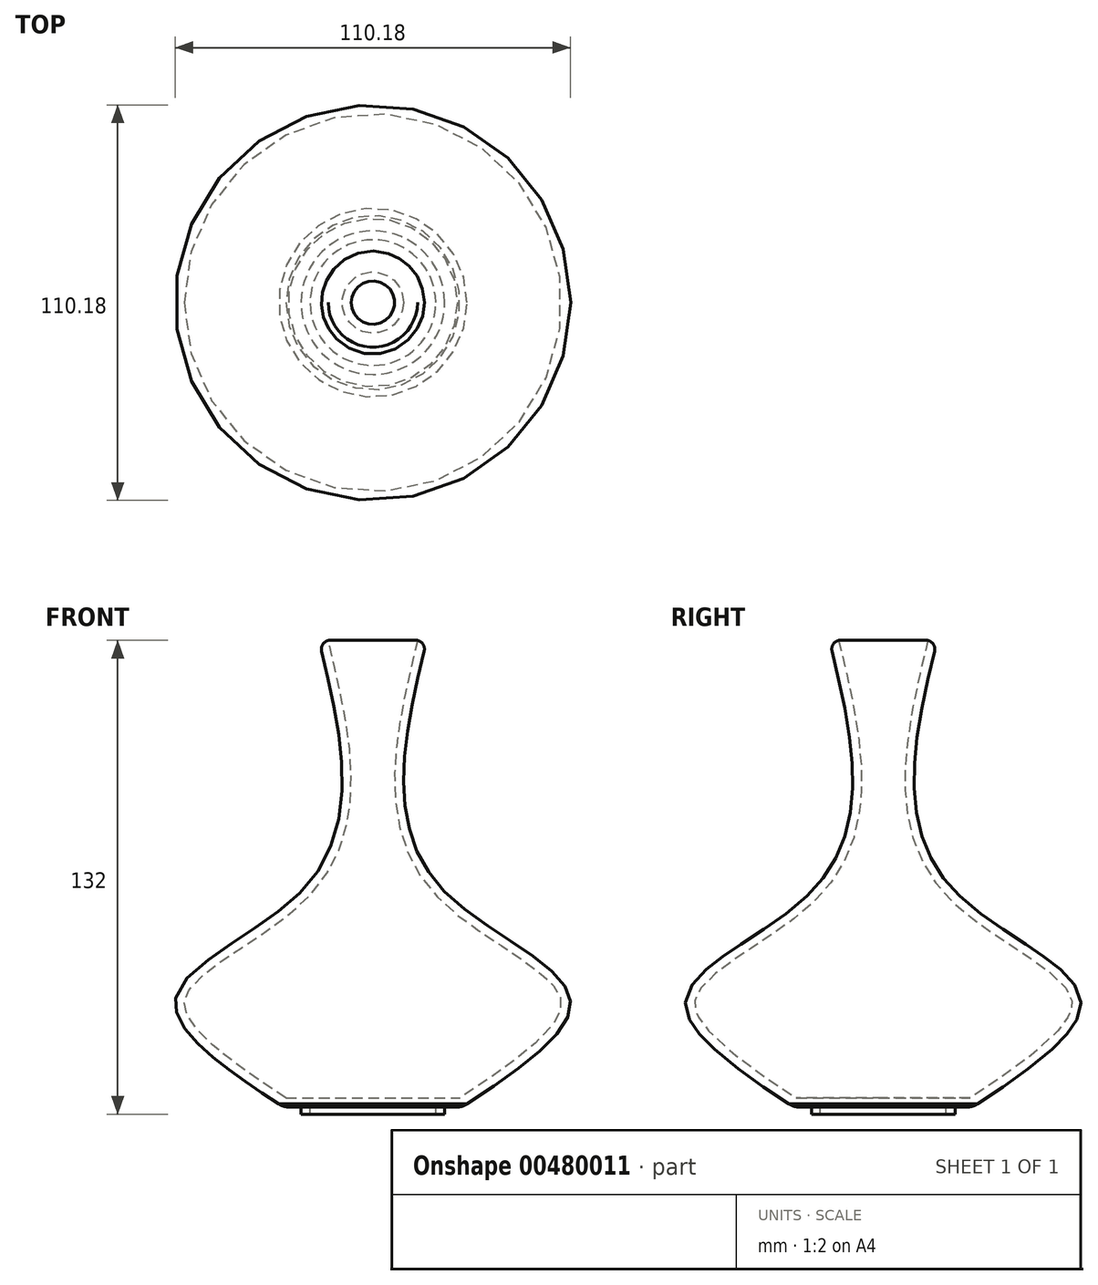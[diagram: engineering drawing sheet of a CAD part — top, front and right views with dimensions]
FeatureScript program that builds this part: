
annotation { "Feature Type Name" : "Feature", "Feature Type Description" : "" }
export const myFeature = defineFeature(function(context is Context, id is Id, definition is map)
    precondition{}
    {
        {
            var Q0;
            Q0=qCreatedBy(makeId("Top.planeOp"),FACE);
            var sketch = newSketch(context, id + "F0", { "sketchPlane" : qUnion([Q0])});
            skCircle(sketch, "E0", {"center": v(0, 0) * mm, "radius": 25 * mm});
            skSolve(sketch);
        }
        {
            var Q0;
            Q0=qCreatedBy(makeId("Top.planeOp"),FACE);
            cPlane(context, id + "F1", {"entities" : qUnion([Q0]), "cplaneType" : CPlaneType.OFFSET, "offset" : 30 * mm, "width" : 150 * mm, "height" : 150 * mm});
        }
        {
            var Q0;
            Q0=qCreatedBy(id+"F1.planeOp",FACE);
            var sketch = newSketch(context, id + "F2", { "sketchPlane" : qUnion([Q0])});
            skCircle(sketch, "E1", {"center": v(0, 0) * mm, "radius": 55 * mm});
            skSolve(sketch);
        }
        {
            var Q0;
            Q0=qCreatedBy(id+"F1.planeOp",FACE);
            cPlane(context, id + "F3", {"entities" : qUnion([Q0]), "cplaneType" : CPlaneType.OFFSET, "offset" : 30 * mm, "width" : 150 * mm, "height" : 150 * mm});
        }
        {
            var Q0;
            Q0=qCreatedBy(id+"F3.planeOp",FACE);
            var sketch = newSketch(context, id + "F4", { "sketchPlane" : qUnion([Q0])});
            skCircle(sketch, "E2", {"center": v(0, 0) * mm, "radius": 20 * mm});
            skSolve(sketch);
        }
        {
            var Q0;
            Q0=qCreatedBy(id+"F3.planeOp",FACE);
            cPlane(context, id + "F5", {"entities" : qUnion([Q0]), "cplaneType" : CPlaneType.OFFSET, "offset" : 70 * mm, "width" : 150 * mm, "height" : 150 * mm});
        }
        {
            var Q0;
            Q0=qCreatedBy(id+"F5.planeOp",FACE);
            var sketch = newSketch(context, id + "F6", { "sketchPlane" : qUnion([Q0])});
            skCircle(sketch, "E3", {"center": v(0, 0) * mm, "radius": 15 * mm});
            skSolve(sketch);
        }
        {
            var Q0;
            Q0=makeQuery(id+"F0.imprint","IMPRINT",FACE,{"disambiguationData":[TD([[makeQuery(id+"F0.imprint","IMPRINT",EDGE,{"derivedFrom":sQuery(id+"F0.wireOp",EDGE,"E0")}),1.0]])]});
            var Q1;
            Q1=makeQuery(id+"F2.imprint","IMPRINT",FACE,{"disambiguationData":[TD([[makeQuery(id+"F2.imprint","IMPRINT",EDGE,{"derivedFrom":sQuery(id+"F2.wireOp",EDGE,"E1")}),1.0]])]});
            var Q2;
            Q2=makeQuery(id+"F4.imprint","IMPRINT",FACE,{"disambiguationData":[TD([[makeQuery(id+"F4.imprint","IMPRINT",EDGE,{"derivedFrom":sQuery(id+"F4.wireOp",EDGE,"E2")}),1.0]])]});
            var Q3;
            Q3=makeQuery(id+"F6.imprint","IMPRINT",FACE,{"disambiguationData":[TD([[makeQuery(id+"F6.imprint","IMPRINT",EDGE,{"derivedFrom":sQuery(id+"F6.wireOp",EDGE,"E3")}),1.0]])]});
            loft(context, id + "F7", {"sheetProfilesArray" : [{ "sheetProfileEntities" : qUnion([Q0]) }, { "sheetProfileEntities" : qUnion([Q1]) }, { "sheetProfileEntities" : qUnion([Q2]) }, { "sheetProfileEntities" : qUnion([Q3]) }]});
        }
        {
            var Q0;
            Q0=makeQuery(id+"F7.opLoft","CAP_FACE",FACE,{"disambiguationData":[OSD([makeQuery(id+"F6.imprint","IMPRINT",FACE,{"disambiguationData":[TD([[makeQuery(id+"F6.imprint","IMPRINT",EDGE,{"derivedFrom":sQuery(id+"F6.wireOp",EDGE,"E3")}),1.0]])]})])],"isStart":true});
            shell(context, id + "F8", {"entities" : qUnion([Q0]), "thickness" : 2.5 * mm});
        }
        {
            var Q0;
            Q0=makeQuery(id+"F7.opLoft","CAP_FACE",FACE,{"disambiguationData":[OSD([makeQuery(id+"F0.imprint","IMPRINT",FACE,{"disambiguationData":[TD([[makeQuery(id+"F0.imprint","IMPRINT",EDGE,{"derivedFrom":sQuery(id+"F0.wireOp",EDGE,"E0")}),1.0]])]})])],"isStart":true});
            var sketch = newSketch(context, id + "F9", { "sketchPlane" : qUnion([Q0])});
            skCircle(sketch, "E4", {"center": v(0, 0) * mm, "radius": 20 * mm});
            skCircle(sketch, "E5", {"center": v(0, 0) * mm, "radius": 17.5 * mm});
            skSolve(sketch);
        }
        {
            var Q0;
            Q0=makeQuery(id+"F9.imprint","IMPRINT",FACE,{"disambiguationData":[TD([[makeQuery(id+"F9.imprint","IMPRINT",EDGE,{"derivedFrom":sQuery(id+"F9.wireOp",EDGE,"E4")}),1.0]])]});
            extrude(context, id + "F10", {"entities" : qUnion([Q0]), "operationType" : NewBodyOperationType.ADD, "depth" : 2 * mm});
        }
        {
            var Q0;
            Q0=makeQuery(id+"F7.opLoft","MID_CAP_EDGE",EDGE,{"disambiguationData":[OSD([sQuery(id+"F0.wireOp",EDGE,"E0")])],"capPos":0.0});
            fillet(context, id + "F11", {"entities" : qUnion([Q0]), "radius" : 5 * mm, "tangentPropagation" : true, "allowEdgeOverflow" : false});
        }
        {
            var Q0;
            Q0=makeQuery(id+"F7.opLoft","MID_CAP_EDGE",EDGE,{"disambiguationData":[OSD([sQuery(id+"F0.wireOp",EDGE,"E0"),sQuery(id+"F6.wireOp",EDGE,"E3")])],"capPos":3.0});
            fillet(context, id + "F12", {"entities" : qUnion([Q0]), "radius" : 2.5 * mm, "tangentPropagation" : true, "allowEdgeOverflow" : false});
        }
    });
